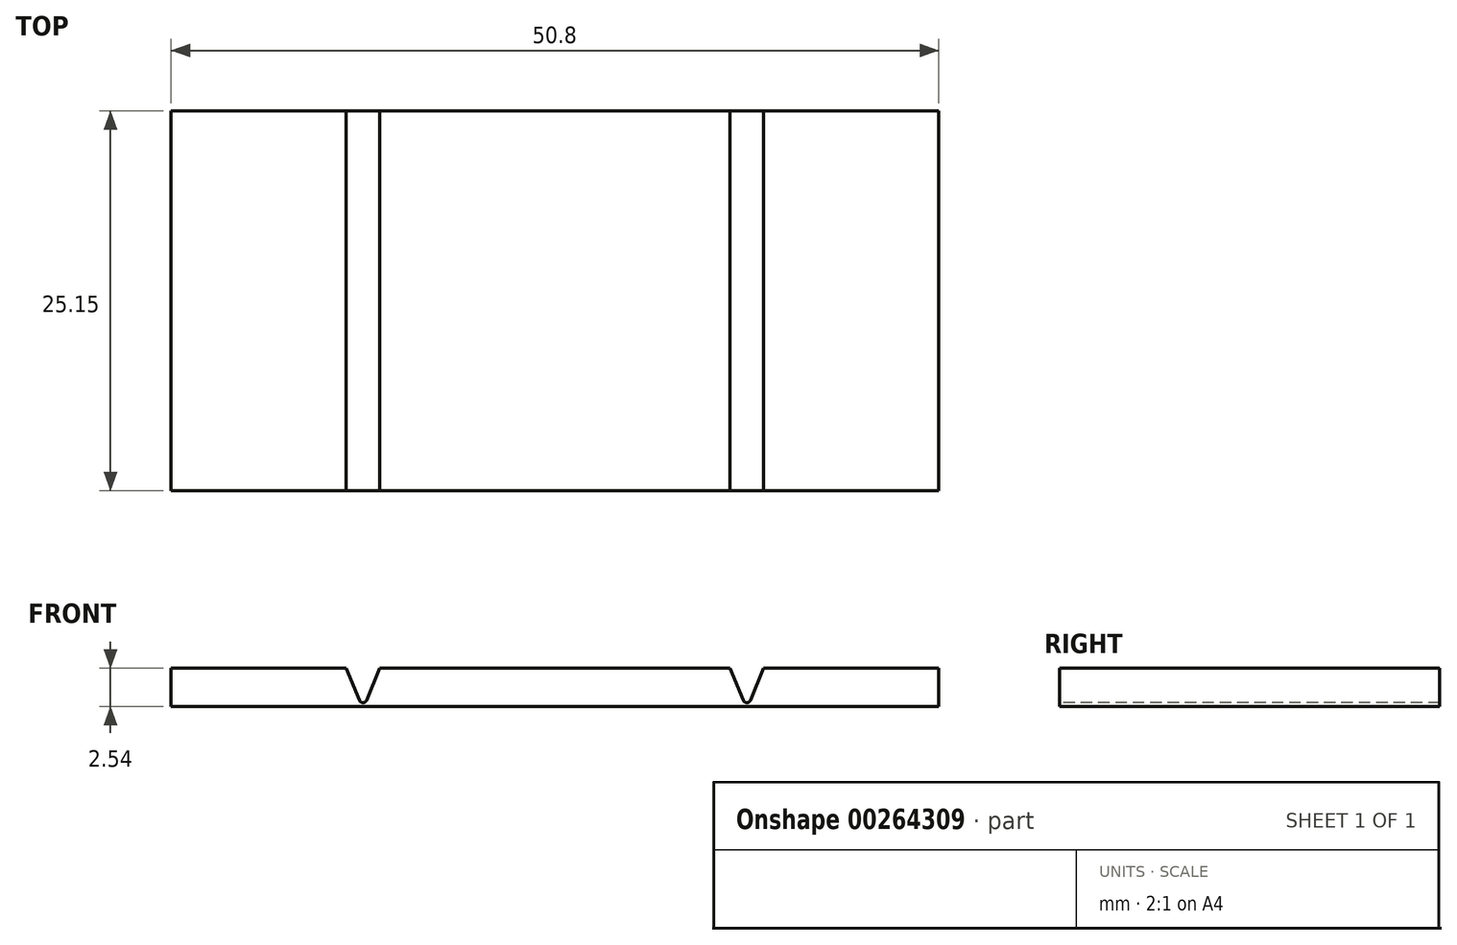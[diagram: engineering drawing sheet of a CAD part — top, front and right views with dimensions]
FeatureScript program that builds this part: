
annotation { "Feature Type Name" : "Feature", "Feature Type Description" : "" }
export const myFeature = defineFeature(function(context is Context, id is Id, definition is map)
    precondition{}
    {
        {
            var Q0;
            Q0=qCreatedBy(makeId("Top.planeOp"),FACE);
            var sketch = newSketch(context, id + "F0", { "sketchPlane" : qUnion([Q0])});
            skLineSegment(sketch, "E0.bottom", {"start": v(0, 0) * mm, "end": v(50.8, 0) * mm});
            skLineSegment(sketch, "E0.top", {"start": v(0, 25.15) * mm, "end": v(50.8, 25.15) * mm});
            skLineSegment(sketch, "E0.left", {"start": v(0, 0) * mm, "end": v(0, 25.15) * mm});
            skLineSegment(sketch, "E0.right", {"start": v(50.8, 0) * mm, "end": v(50.8, 25.15) * mm});
            skLineSegment(sketch, "E1", {"start": v(12.7, 25.15) * mm, "end": v(12.7, 0) * mm});
            skLineSegment(sketch, "E2", {"start": v(38.1, 25.15) * mm, "end": v(38.1, 0) * mm});
            skSolve(sketch);
        }
        {
            var Q0;
            {var subQ0=sQuery(id+"F0.wireOp",EDGE,"E0.left");Q0=makeQuery(id+"F0.imprint","IMPRINT",FACE,{"disambiguationData":[TD([[makeQuery(id+"F0.imprint","IMPRINT",EDGE,{"derivedFrom":subQ0}),-1.0]])]});}
            var Q1;
            {var subQ0=sQuery(id+"F0.wireOp",EDGE,"E1");Q1=makeQuery(id+"F0.imprint","IMPRINT",FACE,{"disambiguationData":[TD([[makeQuery(id+"F0.imprint","IMPRINT",EDGE,{"derivedFrom":subQ0}),1.0]])]});}
            var Q2;
            {var subQ0=sQuery(id+"F0.wireOp",EDGE,"E0.right");Q2=makeQuery(id+"F0.imprint","IMPRINT",FACE,{"disambiguationData":[TD([[makeQuery(id+"F0.imprint","IMPRINT",EDGE,{"derivedFrom":subQ0}),1.0]])]});}
            extrude(context, id + "F1", {"entities" : qUnion([Q0, Q1, Q2]), "depth" : 2.54 * mm});
        }
        {
            var Q0;
            Q0=makeQuery(id+"F1.opExtrude","SWEPT_FACE",FACE,{"disambiguationData":[OSD([sQuery(id+"F0.wireOp",EDGE,"E0.bottom")])]});
            var sketch = newSketch(context, id + "F2", { "sketchPlane" : qUnion([Q0])});
            skLineSegment(sketch, "E3", {"start": v(12.7, 0) * mm, "end": v(12.7, 2.54) * mm, "construction": true});
            skLineSegment(sketch, "E4", {"start": v(11.58, 2.54) * mm, "end": v(12.47, 0.41) * mm});
            skLineSegment(sketch, "E5", {"start": v(12.93, 0.41) * mm, "end": v(13.82, 2.54) * mm});
            skLineSegment(sketch, "E6", {"start": v(13.82, 2.54) * mm, "end": v(11.58, 2.54) * mm});
            skPoint(sketch, "E7.visualSharp", {"position": v(12.7, -0.16) * mm});
            skArc(sketch, "E7.filletArc", {"start": v(12.47, 0.41) * mm, "mid": v(12.7, 0.25) * mm, "end": v(12.93, 0.41) * mm});
            skLineSegment(sketch, "E8.1.0.0", {"start": v(36.98, 2.54) * mm, "end": v(37.87, 0.41) * mm});
            skLineSegment(sketch, "E8.1.0.1", {"start": v(38.1, 0) * mm, "end": v(38.1, 2.54) * mm, "construction": true});
            skPoint(sketch, "E8.1.0.2", {"position": v(38.1, -0.16) * mm});
            skLineSegment(sketch, "E8.1.0.3", {"start": v(38.33, 0.41) * mm, "end": v(39.22, 2.54) * mm});
            skLineSegment(sketch, "E8.1.0.4", {"start": v(39.22, 2.54) * mm, "end": v(36.98, 2.54) * mm});
            skArc(sketch, "E8.1.0.5", {"start": v(37.87, 0.41) * mm, "mid": v(38.1, 0.25) * mm, "end": v(38.33, 0.41) * mm});
            skLineSegment(sketch, "E8.direction1", {"start": v(12.7, -0.16) * mm, "end": v(38.1, -0.16) * mm, "construction": true});
            skSolve(sketch);
        }
        {
            var Q0;
            Q0=makeQuery(id+"F2.imprint","IMPRINT",FACE,{"disambiguationData":[TD([[makeQuery(id+"F2.imprint","IMPRINT",EDGE,{"derivedFrom":sQuery(id+"F2.wireOp",EDGE,"E4")}),1.0]])]});
            var Q1;
            Q1=makeQuery(id+"F2.imprint","IMPRINT",FACE,{"disambiguationData":[TD([[makeQuery(id+"F2.imprint","IMPRINT",EDGE,{"derivedFrom":sQuery(id+"F2.wireOp",EDGE,"E8.1.0.0")}),1.0]])]});
            extrude(context, id + "F3", {"entities" : qUnion([Q0, Q1]), "operationType" : NewBodyOperationType.REMOVE, "endBound" : BoundingType.THROUGH_ALL, "oppositeDirection" : true, "depth" : 25.4 * mm});
        }
    });
